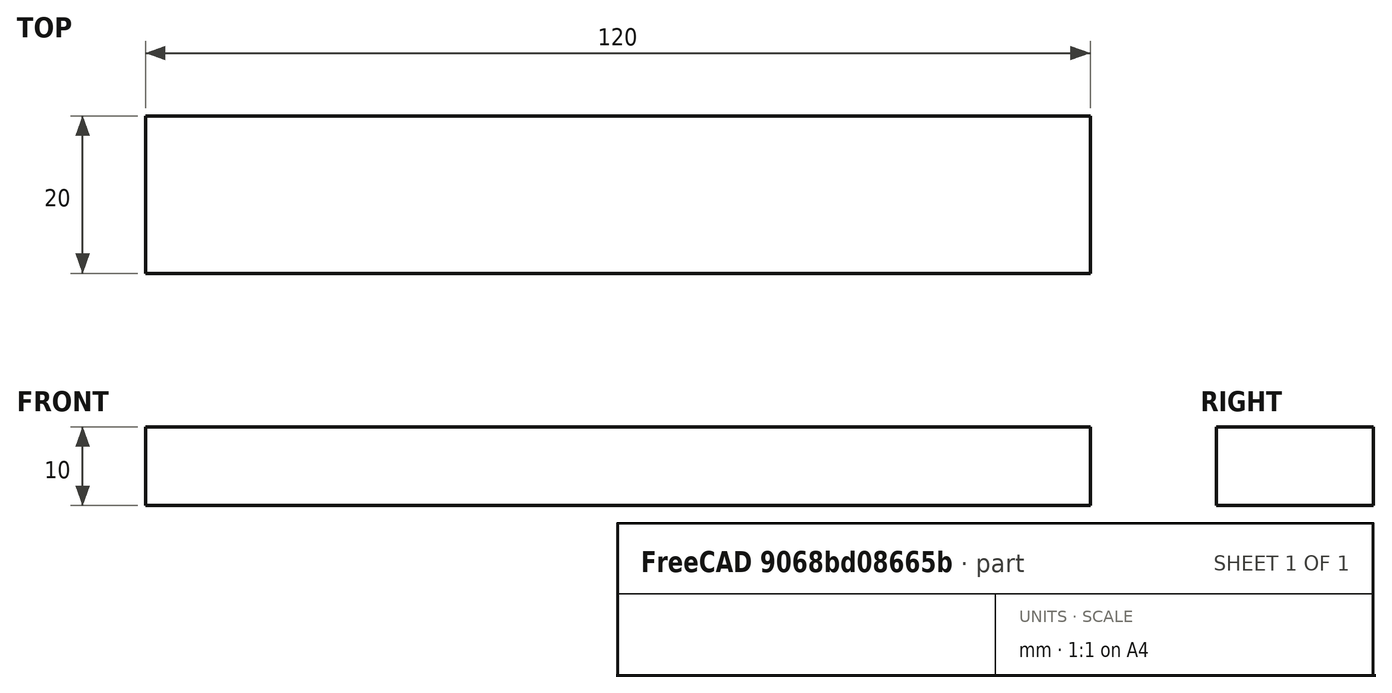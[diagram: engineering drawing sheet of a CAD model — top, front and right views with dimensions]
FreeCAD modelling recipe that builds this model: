
FCSTD DOCUMENT  (FreeCAD 1.0R39319 (Git))
Label: cantilever_beam_model
License: All rights reserved
LicenseURL: https://en.wikipedia.org/wiki/All_rights_reserved
objects: Sketcher::SketchObject×1, PartDesign::Pad×1, PartDesign::Body×1
note: 6 computed .brp shape members not serialized (recipe doc carries the construction recipe); baked Part::Feature solids carry a one-line shape summary decoded from their .brp

FEATURE [Sketcher::SketchObject] Sketch
  ArcFitTolerance = 1e-06
  AttachmentSupport = -> [XY_Plane002]
  FullyConstrained = false
  MakeInternals = false
  MapMode = 5
  sketch-geometry (4):
    g0: LineSegment StartX=-70 StartY=12.0613 StartZ=0 EndX=-70 EndY=-7.93866 EndZ=0
    g1: LineSegment StartX=-70 StartY=-7.93866 StartZ=0 EndX=50 EndY=-7.93866 EndZ=0
    g2: LineSegment StartX=50 StartY=-7.93866 StartZ=0 EndX=50 EndY=12.0613 EndZ=0
    g3: LineSegment StartX=50 StartY=12.0613 StartZ=0 EndX=-70 EndY=12.0613 EndZ=0
  constraints (11):
    c: Coincident(g0,g1)
    c: Coincident(g1,g2)
    c: Coincident(g2,g3)
    c: Coincident(g3,g0)
    c: Vertical(g0)
    c: Vertical(g2)
    c: Horizontal(g1)
    c: Horizontal(g3)
    c: Distance(g0) = 20
    c: Distance(g3) = 120
    c: DistanceX(g2) = 50
FEATURE [PartDesign::Pad] Pad
  Direction = (0,0,1)
  Length = 10
  Length2 = 10
  Profile = -> Sketch
  ReferenceAxis = -> Sketch [N_Axis]
  Refine = true
  Suppressed = false
  Type = 0
FEATURE [PartDesign::Body] Body002
  AllowCompound = false
  Group = -> [Sketch,Pad]
  Origin = -> Origin002
  Tip = -> Pad
